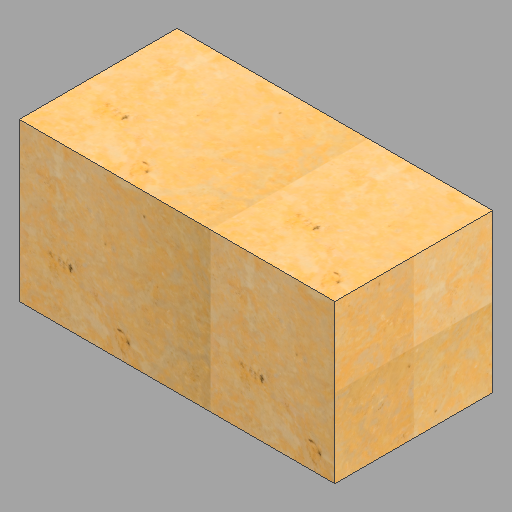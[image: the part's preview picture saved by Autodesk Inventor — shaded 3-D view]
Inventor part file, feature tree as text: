
AUTODESK INVENTOR PART (.ipt)
format: ipt  version: 2023 (Build 270158030, 158C)  size: 395,264 bytes
history: native  units: in
note: dims shown in document units (in); Inventor stores cm internally (conversion verified against a paired STEP export)
features: other x1, extrude x1, sketch x1
ambient origin geometry x8: Origin, YZ Plane, XZ Plane, XY Plane, X Axis, Y Axis, Z Axis, Center Point
bodies: Solid1 (feature_tree)
feature tree (3):
  other  "Block-typ"
  extrude  "Extrusion1"  Depth=24.0in
  sketch  "Sketch1"  dims[d0=24.0in d1=24.0in d2=48.0in d3=0.0in]
